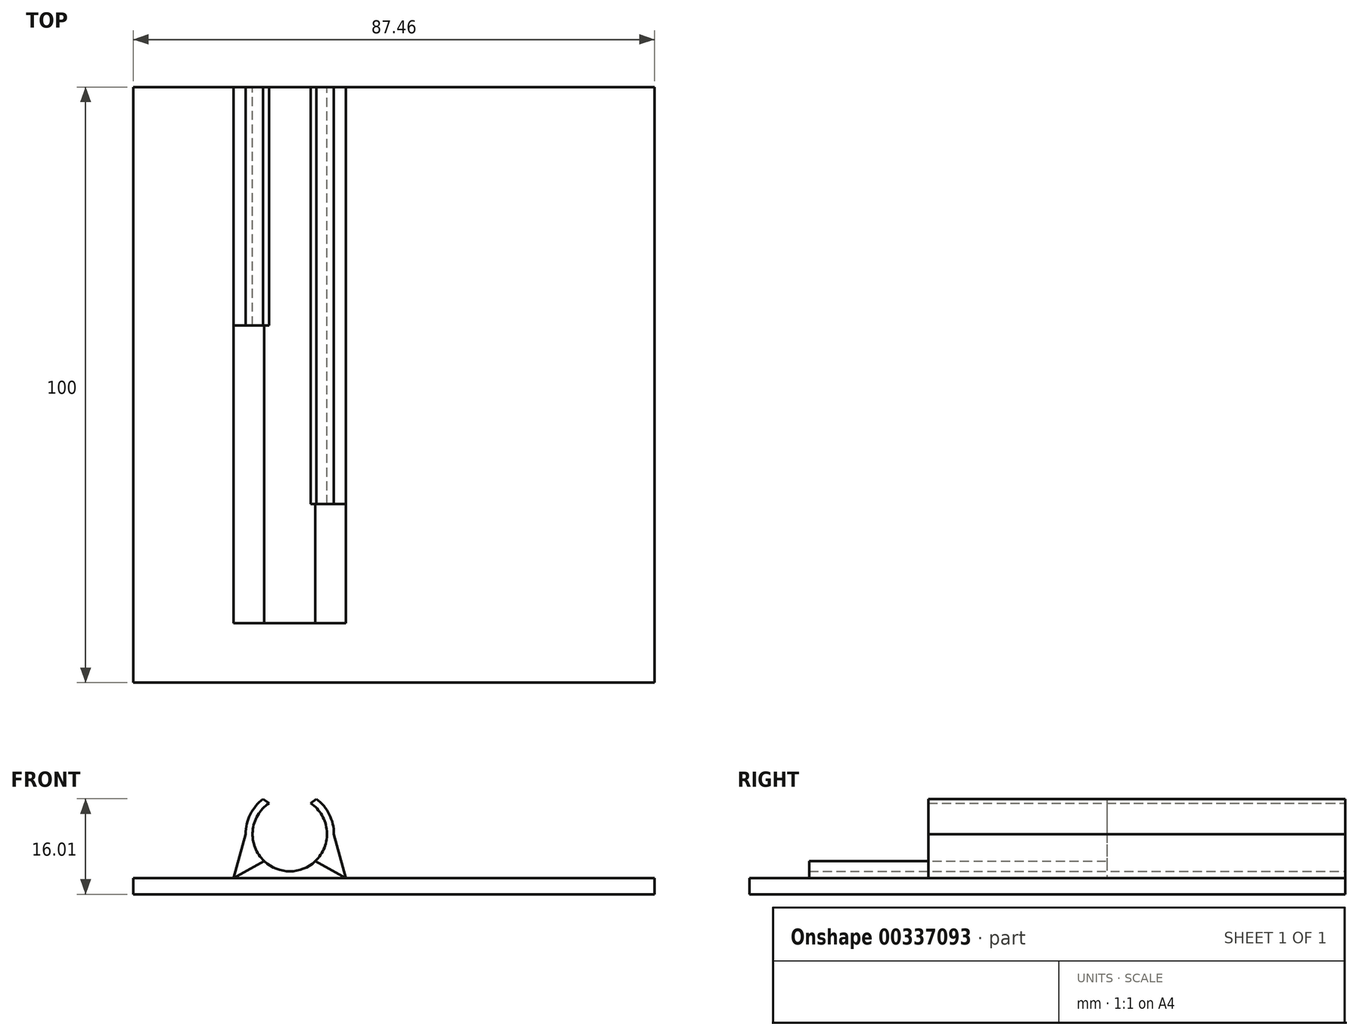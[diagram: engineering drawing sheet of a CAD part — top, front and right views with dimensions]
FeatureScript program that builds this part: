
annotation { "Feature Type Name" : "Feature", "Feature Type Description" : "" }
export const myFeature = defineFeature(function(context is Context, id is Id, definition is map)
    precondition{}
    {
        {
            var Q0;
            Q0=qCreatedBy(makeId("Front.planeOp"),FACE);
            var sketch = newSketch(context, id + "F0", { "sketchPlane" : qUnion([Q0])});
            skArc(sketch, "E0", {"start": v(-3.5, 5.18) * mm, "mid": v(0, -6.25) * mm, "end": v(3.5, 5.18) * mm});
            skPoint(sketch, "E1", {"position": v(3.5, 5.18) * mm});
            skPoint(sketch, "E2.MirrorP", {"position": v(-3.5, 5.18) * mm});
            skArc(sketch, "E3", {"start": v(-4.47, 5.9) * mm, "mid": v(0, -7.4) * mm, "end": v(4.47, 5.9) * mm});
            skPoint(sketch, "E4", {"position": v(-4.47, 5.9) * mm});
            skPoint(sketch, "E5.MirrorP", {"position": v(4.47, 5.9) * mm});
            skLineSegment(sketch, "E6", {"start": v(-4.47, 5.9) * mm, "end": v(-3.5, 5.18) * mm});
            skLineSegment(sketch, "E7.MirrorCS", {"start": v(4.47, 5.9) * mm, "end": v(3.5, 5.18) * mm});
            skLineSegment(sketch, "E8.left", {"start": v(0, -7.4) * mm, "end": v(0, -10.1) * mm});
            skLineSegment(sketch, "E9.MirrorCS", {"start": v(0, -7.4) * mm, "end": v(61.2, -7.4) * mm});
            skLineSegment(sketch, "E10.MirrorCS", {"start": v(0, -10.1) * mm, "end": v(61.2, -10.1) * mm});
            skLineSegment(sketch, "E11.MirrorCS", {"start": v(61.2, -7.4) * mm, "end": v(61.2, -10.1) * mm});
            skLineSegment(sketch, "E12", {"start": v(-7.4, 0) * mm, "end": v(-9.42, -7.4) * mm});
            skLineSegment(sketch, "E13.MirrorCS", {"start": v(7.4, 0) * mm, "end": v(9.42, -7.4) * mm});
            skLineSegment(sketch, "E14", {"start": v(-4.27, -4.56) * mm, "end": v(-9.42, -7.4) * mm});
            skLineSegment(sketch, "E15.MirrorCS", {"start": v(4.27, -4.56) * mm, "end": v(9.42, -7.4) * mm});
            skLineSegment(sketch, "E16.bottom", {"start": v(0, -7.4) * mm, "end": v(-26.26, -7.4) * mm});
            skLineSegment(sketch, "E16.top", {"start": v(0, -10.1) * mm, "end": v(-26.26, -10.1) * mm});
            skLineSegment(sketch, "E16.right", {"start": v(-26.26, -7.4) * mm, "end": v(-26.26, -10.1) * mm});
            skLineSegment(sketch, "E17.bottom", {"start": v(61.2, -7.4) * mm, "end": v(57.72, -7.4) * mm});
            skLineSegment(sketch, "E17.top", {"start": v(61.2, 35.19) * mm, "end": v(57.72, 35.19) * mm});
            skLineSegment(sketch, "E17.left", {"start": v(61.2, -7.4) * mm, "end": v(61.2, 35.19) * mm});
            skLineSegment(sketch, "E17.right", {"start": v(57.72, -7.4) * mm, "end": v(57.72, 35.19) * mm});
            skSolve(sketch);
        }
        {
            var Q0;
            {var subQ0=sQuery(id+"F0.wireOp",EDGE,"E14");var subQ1=sQuery(id+"F0.wireOp",EDGE,"E0");var subQ2=makeQuery(id+"F0.imprint","INTERSECT",VERTEX,{"derivedFrom":[subQ1,subQ0]});Q0=makeQuery(id+"F0.imprint","IMPRINT",FACE,{"disambiguationData":[TD([[makeQuery(id+"F0.imprint","IMPRINT",EDGE,{"disambiguationData":[TD([[subQ2,-1.0]])],"derivedFrom":subQ1}),-1.0]])]});}
            var Q1;
            {var subQ1=sQuery(id+"F0.wireOp",EDGE,"E3");var subQ3=sQuery(id+"F0.wireOp",EDGE,"E15.MirrorCS");var subQ4=makeQuery(id+"F0.imprint","INTERSECT",VERTEX,{"derivedFrom":[subQ1,subQ3]});Q1=makeQuery(id+"F0.imprint","IMPRINT",FACE,{"disambiguationData":[TD([[makeQuery(id+"F0.imprint","IMPRINT",EDGE,{"disambiguationData":[TD([[subQ4,-1.0]])],"derivedFrom":subQ3}),-1.0]])]});}
            var Q2;
            {var subQ1=sQuery(id+"F0.wireOp",EDGE,"E3");var subQ3=sQuery(id+"F0.wireOp",EDGE,"E14");var subQ4=makeQuery(id+"F0.imprint","INTERSECT",VERTEX,{"derivedFrom":[subQ1,subQ3]});Q2=makeQuery(id+"F0.imprint","IMPRINT",FACE,{"disambiguationData":[TD([[makeQuery(id+"F0.imprint","IMPRINT",EDGE,{"disambiguationData":[TD([[subQ4,-1.0]])],"derivedFrom":subQ3}),1.0]])]});}
            var Q3;
            Q3=makeQuery(id+"F0.imprint","IMPRINT",FACE,{"disambiguationData":[TD([[makeQuery(id+"F0.imprint","IMPRINT",EDGE,{"derivedFrom":sQuery(id+"F0.wireOp",EDGE,"E8.top")}),-1.0]])]});
            var Q4;
            {var subQ3=sQuery(id+"F0.wireOp",EDGE,"E8.left");Q4=makeQuery(id+"F0.imprint","IMPRINT",FACE,{"disambiguationData":[TD([[makeQuery(id+"F0.imprint","IMPRINT",EDGE,{"derivedFrom":subQ3}),1.0]])]});}
            extrude(context, id + "F1", {"entities" : qUnion([Q0, Q1, Q2, Q3, Q4]), "depth" : 90 * mm});
        }
        {
            var Q0;
            {var subQ0=sQuery(id+"F0.wireOp",EDGE,"E12");Q0=makeQuery(id+"F0.imprint","IMPRINT",FACE,{"disambiguationData":[TD([[makeQuery(id+"F0.imprint","IMPRINT",EDGE,{"derivedFrom":subQ0}),1.0]])]});}
            var Q1;
            {var subQ0=sQuery(id+"F0.wireOp",EDGE,"E6");Q1=makeQuery(id+"F0.imprint","IMPRINT",FACE,{"disambiguationData":[TD([[makeQuery(id+"F0.imprint","IMPRINT",EDGE,{"derivedFrom":subQ0}),-1.0]])]});}
            var Q2;
            {var subQ0=sQuery(id+"F0.wireOp",EDGE,"E7.MirrorCS");Q2=makeQuery(id+"F0.imprint","IMPRINT",FACE,{"disambiguationData":[TD([[makeQuery(id+"F0.imprint","IMPRINT",EDGE,{"derivedFrom":subQ0}),1.0]])]});}
            var Q3;
            {var subQ0=sQuery(id+"F0.wireOp",EDGE,"E13.MirrorCS");Q3=makeQuery(id+"F0.imprint","IMPRINT",FACE,{"disambiguationData":[TD([[makeQuery(id+"F0.imprint","IMPRINT",EDGE,{"derivedFrom":subQ0}),-1.0]])]});}
            extrude(context, id + "F2", {"entities" : qUnion([Q0, Q1, Q2, Q3]), "operationType" : NewBodyOperationType.ADD, "depth" : 40 * mm});
        }
        {
            var Q0;
            Q0=makeQuery(id+"F0.imprint","IMPRINT",FACE,{"disambiguationData":[TD([[makeQuery(id+"F0.imprint","IMPRINT",EDGE,{"derivedFrom":sQuery(id+"F0.wireOp",EDGE,"E16.top")}),-1.0]])]});
            var Q1;
            Q1=makeQuery(id+"F0.imprint","IMPRINT",FACE,{"disambiguationData":[TD([[makeQuery(id+"F0.imprint","IMPRINT",EDGE,{"derivedFrom":sQuery(id+"F0.wireOp",EDGE,"E10.MirrorCS")}),1.0]])]});
            var Q2;
            Q2=makeQuery(id+"F0.imprint","IMPRINT",FACE,{"disambiguationData":[TD([[makeQuery(id+"F0.imprint","IMPRINT",EDGE,{"derivedFrom":sQuery(id+"F0.wireOp",EDGE,"E17.bottom")}),-1.0]])]});
            extrude(context, id + "F3", {"entities" : qUnion([Q0, Q1, Q2]), "operationType" : NewBodyOperationType.ADD, "depth" : 100 * mm});
        }
        {
            var Q0;
            {var subQ0=sQuery(id+"F0.wireOp",EDGE,"E7.MirrorCS");Q0=makeQuery(id+"F0.imprint","IMPRINT",FACE,{"disambiguationData":[TD([[makeQuery(id+"F0.imprint","IMPRINT",EDGE,{"derivedFrom":subQ0}),1.0]])]});}
            var Q1;
            {var subQ0=sQuery(id+"F0.wireOp",EDGE,"E13.MirrorCS");Q1=makeQuery(id+"F0.imprint","IMPRINT",FACE,{"disambiguationData":[TD([[makeQuery(id+"F0.imprint","IMPRINT",EDGE,{"derivedFrom":subQ0}),-1.0]])]});}
            extrude(context, id + "F4", {"entities" : qUnion([Q0, Q1]), "operationType" : NewBodyOperationType.ADD, "depth" : 70 * mm});
        }
    });
